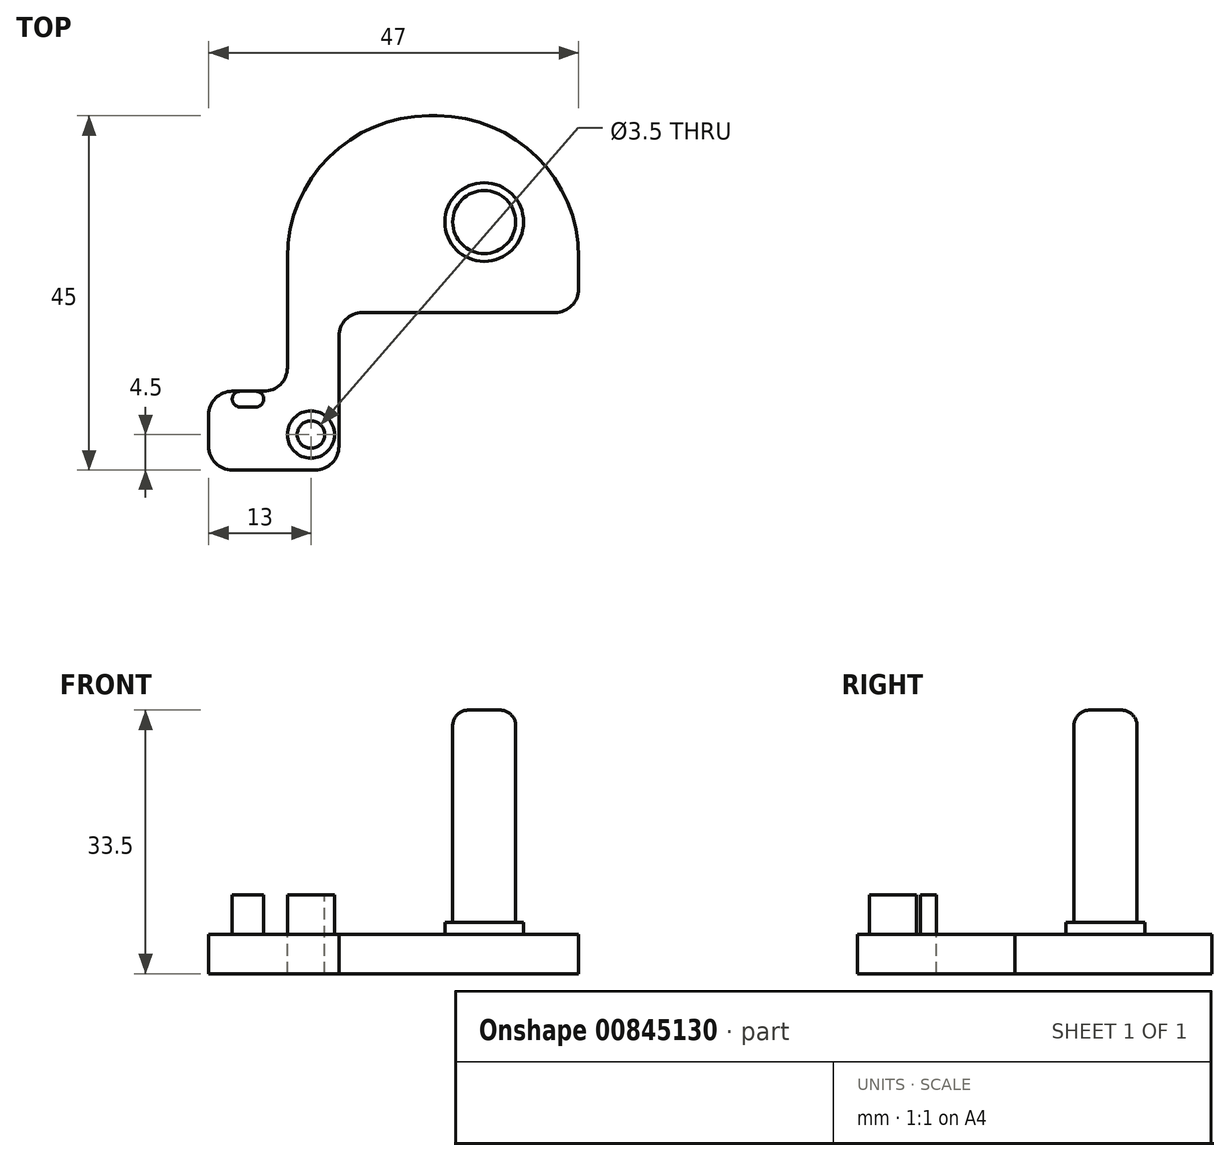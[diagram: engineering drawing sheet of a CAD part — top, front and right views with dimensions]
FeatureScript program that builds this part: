
annotation { "Feature Type Name" : "Feature", "Feature Type Description" : "" }
export const myFeature = defineFeature(function(context is Context, id is Id, definition is map)
    precondition{}
    {
        {
            var Q0;
            Q0=qCreatedBy(makeId("Top.planeOp"),FACE);
            var sketch = newSketch(context, id + "F0", { "sketchPlane" : qUnion([Q0])});
            skLineSegment(sketch, "E0.bottom", {"start": v(25, 25) * mm, "end": v(-25, 25) * mm, "construction": true});
            skLineSegment(sketch, "E0.top", {"start": v(25, -25) * mm, "end": v(-25, -25) * mm, "construction": true});
            skLineSegment(sketch, "E0.left", {"start": v(25, 25) * mm, "end": v(25, -25) * mm, "construction": true});
            skLineSegment(sketch, "E0.right", {"start": v(-25, 25) * mm, "end": v(-25, -25) * mm, "construction": true});
            skPoint(sketch, "E0.middle", {"position": v(0, 0) * mm});
            skLineSegment(sketch, "E1.bottom", {"start": v(-25, 0) * mm, "end": v(25, 0) * mm, "construction": true});
            skLineSegment(sketch, "E1.top", {"start": v(-25, 55) * mm, "end": v(25, 55) * mm, "construction": true});
            skLineSegment(sketch, "E1.left", {"start": v(-25, 0) * mm, "end": v(-25, 55) * mm, "construction": true});
            skLineSegment(sketch, "E1.right", {"start": v(25, 0) * mm, "end": v(25, 55) * mm, "construction": true});
            skCircle(sketch, "E2", {"center": v(0, 0) * mm, "radius": 19 * mm, "construction": true});
            skCircle(sketch, "E3", {"center": v(-22, 0) * mm, "radius": 1.75 * mm});
            skLineSegment(sketch, "E4", {"start": v(-25, -4.5) * mm, "end": v(-18.46, -4.5) * mm});
            skCircle(sketch, "E5", {"center": v(0, 0) * mm, "radius": 15 * mm, "construction": true});
            skCircle(sketch, "E6", {"center": v(0, 27) * mm, "radius": 12 * mm, "construction": true});
            skLineSegment(sketch, "E7", {"start": v(-25, -4.5) * mm, "end": v(-25, 40.5) * mm});
            skLineSegment(sketch, "E8", {"start": v(-25, 40.5) * mm, "end": v(12, 40.5) * mm});
            skLineSegment(sketch, "E9", {"start": v(12, 40.5) * mm, "end": v(12, 15.5) * mm});
            skLineSegment(sketch, "E10", {"start": v(12, 15.5) * mm, "end": v(-25, 15.5) * mm});
            skLineSegment(sketch, "E11", {"start": v(-18.46, -4.5) * mm, "end": v(-18.46, 15.5) * mm});
            skCircle(sketch, "E12", {"center": v(0, 27) * mm, "radius": 4 * mm});
            skCircle(sketch, "E13", {"center": v(0, 27) * mm, "radius": 5 * mm});
            skLineSegment(sketch, "E14.bottom", {"start": v(-25, -4.5) * mm, "end": v(-35, -4.5) * mm});
            skLineSegment(sketch, "E14.top", {"start": v(-25, 5.5) * mm, "end": v(-35, 5.5) * mm});
            skLineSegment(sketch, "E14.left", {"start": v(-25, -4.5) * mm, "end": v(-25, 5.5) * mm});
            skLineSegment(sketch, "E14.right", {"start": v(-35, -4.5) * mm, "end": v(-35, 5.5) * mm});
            skSolve(sketch);
        }
        {
            var Q0;
            Q0 = qSketchRegion(id + "F0", true);
            var Q1;
            Q1=makeQuery(id+"F0.imprint","IMPRINT",FACE,{"disambiguationData":[TD([[makeQuery(id+"F0.imprint","IMPRINT",EDGE,{"derivedFrom":sQuery(id+"F0.wireOp",EDGE,"E12")}),1.0]])]});
            var Q2;
            Q2=makeQuery(id+"F0.imprint","IMPRINT",FACE,{"disambiguationData":[TD([[makeQuery(id+"F0.imprint","IMPRINT",EDGE,{"derivedFrom":sQuery(id+"F0.wireOp",EDGE,"E12")}),-1.0]])]});
            extrude(context, id + "F1", {"entities" : qUnion([Q0, Q1, Q2]), "oppositeDirection" : true, "depth" : 5 * mm, "offsetDistance" : 25 * mm});
        }
        {
            var Q0;
            Q0=makeQuery(id+"F0.imprint","IMPRINT",FACE,{"disambiguationData":[TD([[makeQuery(id+"F0.imprint","IMPRINT",EDGE,{"derivedFrom":sQuery(id+"F0.wireOp",EDGE,"E12")}),1.0]])]});
            var Q1;
            Q1=makeQuery(id+"F0.imprint","IMPRINT",FACE,{"disambiguationData":[TD([[makeQuery(id+"F0.imprint","IMPRINT",EDGE,{"derivedFrom":sQuery(id+"F0.wireOp",EDGE,"E12")}),-1.0]])]});
            extrude(context, id + "F2", {"entities" : qUnion([Q0, Q1]), "operationType" : NewBodyOperationType.ADD, "depth" : 1.5 * mm, "offsetDistance" : 25 * mm});
        }
        {
            var Q0;
            Q0=makeQuery(id+"F2.opExtrude","CAP_FACE",FACE,{"disambiguationData":[OSD([sQuery(id+"F0.wireOp",EDGE,"E13")])],"isStart":false});
            var sketch = newSketch(context, id + "F3", { "sketchPlane" : qUnion([Q0])});
            skCircle(sketch, "E15", {"center": v(0, 27) * mm, "radius": 4 * mm});
            skSolve(sketch);
        }
        {
            var Q0;
            Q0 = qSketchRegion(id + "F3", true);
            extrude(context, id + "F4", {"entities" : qUnion([Q0]), "operationType" : NewBodyOperationType.ADD, "depth" : 27 * mm, "offsetDistance" : 25 * mm});
        }
        {
            var Q0;
            Q0=makeQuery(id+"F4.opExtrude","CAP_FACE",FACE,{"disambiguationData":[OSD([sQuery(id+"F3.wireOp",EDGE,"E15")])],"isStart":false});
            fillet(context, id + "F5", {"entities" : qUnion([Q0]), "radius" : 2 * mm, "tangentPropagation" : true, "allowEdgeOverflow" : false});
        }
        {
            var Q0;
            Q0=makeQuery(id+"F1.opExtrude","SWEPT_EDGE",EDGE,{"disambiguationData":[OSD([sQuery(id+"F0.wireOp",EDGE,"E7"),sQuery(id+"F0.wireOp",EDGE,"E8")])]});
            var Q1;
            Q1=makeQuery(id+"F1.opExtrude","SWEPT_EDGE",EDGE,{"disambiguationData":[OSD([sQuery(id+"F0.wireOp",EDGE,"E8"),sQuery(id+"F0.wireOp",EDGE,"E9")])]});
            fillet(context, id + "F6", {"entities" : qUnion([Q0, Q1]), "radius" : 18 * mm, "tangentPropagation" : true, "allowEdgeOverflow" : false});
        }
        {
            var Q0;
            Q0=makeQuery(id+"F1.opExtrude","CAP_FACE",FACE,{"disambiguationData":[OSD([sQuery(id+"F0.wireOp",EDGE,"E3"),sQuery(id+"F0.wireOp",EDGE,"E4"),sQuery(id+"F0.wireOp",EDGE,"E7"),sQuery(id+"F0.wireOp",EDGE,"E8"),sQuery(id+"F0.wireOp",EDGE,"E9"),sQuery(id+"F0.wireOp",EDGE,"E10"),sQuery(id+"F0.wireOp",EDGE,"E11")])],"isStart":true});
            var sketch = newSketch(context, id + "F7", { "sketchPlane" : qUnion([Q0])});
            skCircle(sketch, "E16", {"center": v(-22, 0) * mm, "radius": 3 * mm});
            skSolve(sketch);
        }
        {
            var Q0;
            Q0=makeQuery(id+"F7.imprint","IMPRINT",FACE,{"disambiguationData":[TD([[makeQuery(id+"F7.imprint","IMPRINT",EDGE,{"derivedFrom":sQuery(id+"F7.wireOp",EDGE,"E16")}),1.0]])]});
            extrude(context, id + "F8", {"entities" : qUnion([Q0]), "operationType" : NewBodyOperationType.ADD, "depth" : 5 * mm, "offsetDistance" : 25 * mm});
        }
        {
            var Q0;
            Q0=makeQuery(id+"F1.opExtrude","SWEPT_EDGE",EDGE,{"disambiguationData":[OSD([sQuery(id+"F0.wireOp",EDGE,"E7"),sQuery(id+"F0.wireOp",EDGE,"E14.top"),sQuery(id+"F0.wireOp",EDGE,"E14.left")])]});
            var Q1;
            Q1=makeQuery(id+"F1.opExtrude","SWEPT_EDGE",EDGE,{"disambiguationData":[OSD([sQuery(id+"F0.wireOp",EDGE,"E14.top"),sQuery(id+"F0.wireOp",EDGE,"E14.right")])]});
            var Q2;
            Q2=makeQuery(id+"F1.opExtrude","SWEPT_EDGE",EDGE,{"disambiguationData":[OSD([sQuery(id+"F0.wireOp",EDGE,"E14.bottom"),sQuery(id+"F0.wireOp",EDGE,"E14.right")])]});
            var Q3;
            Q3=makeQuery(id+"F1.opExtrude","SWEPT_EDGE",EDGE,{"disambiguationData":[OSD([sQuery(id+"F0.wireOp",EDGE,"E4"),sQuery(id+"F0.wireOp",EDGE,"E11")])]});
            var Q4;
            Q4=makeQuery(id+"F1.opExtrude","SWEPT_EDGE",EDGE,{"disambiguationData":[OSD([sQuery(id+"F0.wireOp",EDGE,"E10"),sQuery(id+"F0.wireOp",EDGE,"E11")])]});
            var Q5;
            Q5=makeQuery(id+"F1.opExtrude","SWEPT_EDGE",EDGE,{"disambiguationData":[OSD([sQuery(id+"F0.wireOp",EDGE,"E9"),sQuery(id+"F0.wireOp",EDGE,"E10")])]});
            fillet(context, id + "F9", {"entities" : qUnion([Q0, Q1, Q2, Q3, Q4, Q5]), "radius" : 3 * mm, "tangentPropagation" : true, "allowEdgeOverflow" : false});
        }
        {
            var Q0;
            Q0=makeQuery(id+"F1.opExtrude","CAP_FACE",FACE,{"disambiguationData":[OSD([sQuery(id+"F0.wireOp",EDGE,"E3"),sQuery(id+"F0.wireOp",EDGE,"E4"),sQuery(id+"F0.wireOp",EDGE,"E7"),sQuery(id+"F0.wireOp",EDGE,"E8"),sQuery(id+"F0.wireOp",EDGE,"E9"),sQuery(id+"F0.wireOp",EDGE,"E10"),sQuery(id+"F0.wireOp",EDGE,"E11"),sQuery(id+"F0.wireOp",EDGE,"E14.bottom"),sQuery(id+"F0.wireOp",EDGE,"E14.top"),sQuery(id+"F0.wireOp",EDGE,"E14.right")])],"isStart":true});
            var sketch = newSketch(context, id + "F10", { "sketchPlane" : qUnion([Q0])});
            skLineSegment(sketch, "E17.bottom", {"start": v(-32, 5.5) * mm, "end": v(-28, 5.5) * mm});
            skLineSegment(sketch, "E17.top", {"start": v(-32, 3.5) * mm, "end": v(-28, 3.5) * mm});
            skLineSegment(sketch, "E17.left", {"start": v(-32, 5.5) * mm, "end": v(-32, 3.5) * mm});
            skLineSegment(sketch, "E17.right", {"start": v(-28, 5.5) * mm, "end": v(-28, 3.5) * mm});
            skSolve(sketch);
        }
        {
            var Q0;
            Q0 = qSketchRegion(id + "F10", true);
            extrude(context, id + "F11", {"entities" : qUnion([Q0]), "operationType" : NewBodyOperationType.ADD, "depth" : 5 * mm, "offsetDistance" : 25 * mm});
        }
        {
            var Q0;
            Q0=makeQuery(id+"F11.opExtrude","SWEPT_EDGE",EDGE,{"disambiguationData":[OSD([sQuery(id+"F0.wireOp",EDGE,"E3"),sQuery(id+"F0.wireOp",EDGE,"E4"),sQuery(id+"F0.wireOp",EDGE,"E7"),sQuery(id+"F0.wireOp",EDGE,"E8"),sQuery(id+"F0.wireOp",EDGE,"E9"),sQuery(id+"F0.wireOp",EDGE,"E10"),sQuery(id+"F0.wireOp",EDGE,"E11"),sQuery(id+"F0.wireOp",EDGE,"E14.bottom"),sQuery(id+"F0.wireOp",EDGE,"E14.top"),sQuery(id+"F0.wireOp",EDGE,"E14.right"),sQuery(id+"F10.wireOp",EDGE,"E17.bottom"),sQuery(id+"F10.wireOp",EDGE,"E17.left")])]});
            var Q1;
            Q1=makeQuery(id+"F11.opExtrude","SWEPT_EDGE",EDGE,{"disambiguationData":[OSD([sQuery(id+"F10.wireOp",EDGE,"E17.top"),sQuery(id+"F10.wireOp",EDGE,"E17.left")])]});
            var Q2;
            Q2=makeQuery(id+"F11.opExtrude","SWEPT_EDGE",EDGE,{"disambiguationData":[OSD([sQuery(id+"F10.wireOp",EDGE,"E17.top"),sQuery(id+"F10.wireOp",EDGE,"E17.right")])]});
            var Q3;
            Q3=makeQuery(id+"F11.opExtrude","SWEPT_EDGE",EDGE,{"disambiguationData":[OSD([sQuery(id+"F0.wireOp",EDGE,"E3"),sQuery(id+"F0.wireOp",EDGE,"E4"),sQuery(id+"F0.wireOp",EDGE,"E7"),sQuery(id+"F0.wireOp",EDGE,"E8"),sQuery(id+"F0.wireOp",EDGE,"E9"),sQuery(id+"F0.wireOp",EDGE,"E10"),sQuery(id+"F0.wireOp",EDGE,"E11"),sQuery(id+"F0.wireOp",EDGE,"E14.bottom"),sQuery(id+"F0.wireOp",EDGE,"E14.top"),sQuery(id+"F0.wireOp",EDGE,"E14.left"),sQuery(id+"F0.wireOp",EDGE,"E14.right"),sQuery(id+"F10.wireOp",EDGE,"E17.bottom"),sQuery(id+"F10.wireOp",EDGE,"E17.right")])]});
            fillet(context, id + "F12", {"entities" : qUnion([Q0, Q1, Q2, Q3]), "radius" : 1 * mm, "tangentPropagation" : true, "allowEdgeOverflow" : false});
        }
    });
